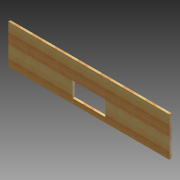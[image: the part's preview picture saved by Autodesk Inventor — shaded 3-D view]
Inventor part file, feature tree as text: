
AUTODESK INVENTOR PART (.ipt)
format: ipt  version: 2012 (Build 160160000, 160)  size: 97,792 bytes
history: native  units: in
note: dims shown in document units (in); Inventor stores cm internally (conversion verified against a paired STEP export)
features: extrude x1, fillet x1, sketch x1
ambient origin geometry x8: Origin, YZ Plane, XZ Plane, XY Plane, X Axis, Y Axis, Z Axis, Center Point
bodies: Solid1 (feature_tree)
feature tree (3):
  extrude  "Extrusion1"  Depth=9.0in
  fillet  "Fillet1"  Radius=0.5in
  sketch  "Sketch1"  dims[d0=37.0in d1=9.0in d2=0.5in d3=0.0in d4=14.75in d5=14.75in d6=7.5in d7=3.5in d8=1.125in d9=0.125in]
